# Revit family: KBE d=800_Precast-Console Beam_Spæncom
name_source: partatom
category: Structural Framing
revit_build: Autodesk Revit 2014 (Build: 20130308_1515(x64)
units: mm (PartAtom-declared; Revit-internal decimal feet)

## types (9) — shared parameters
Base width = 360 mm  [stored 1.1811 ft]
Height console = 800 mm  [stored 2.62467 ft]
Manufacturer = Spæncom
Width (bjælkekroppen) = 310 mm  [stored 1.01706 ft]
Width console = 150 mm

## per-type parameters (varying)
| type | Height (bjælkekroppen) | Height element |
| KBE 102/22 | 220 mm  [stored 0.721785 ft] | 1020 mm  [stored 3.34646 ft] |
| KBE 107/27 | 270 mm  [stored 0.885827 ft] | 1070 mm  [stored 3.5105 ft] |
| KBE 110/30 | 300 mm | 1100 mm |
| KBE 112/32 | 320 mm  [stored 1.04987 ft] | 1120 mm  [stored 3.67454 ft] |
| KBE 117/37 | 370 mm  [stored 1.21391 ft] | 1170 mm  [stored 3.83858 ft] |
| KBE 120/40 | 400 mm  [stored 1.31234 ft] | 1200 mm |
| KBE 130/50 | 500 mm  [stored 1.64042 ft] | 1300 mm  [stored 4.26509 ft] |
| KBE 140/60 | 600 mm | 1400 mm  [stored 4.59318 ft] |
| KBE 98/18 | 180 mm  [stored 0.590551 ft] | 980 mm  [stored 3.21522 ft] |

note: column(s) folded — value = type name in every type: Model

note: [stored X ft] marks values corroborated as IEEE doubles in the binary element streams (Revit-internal decimal feet)

## geometry (parser evidence)
native form markers: Sweep x1
no freeform markers — native parametric forms only
